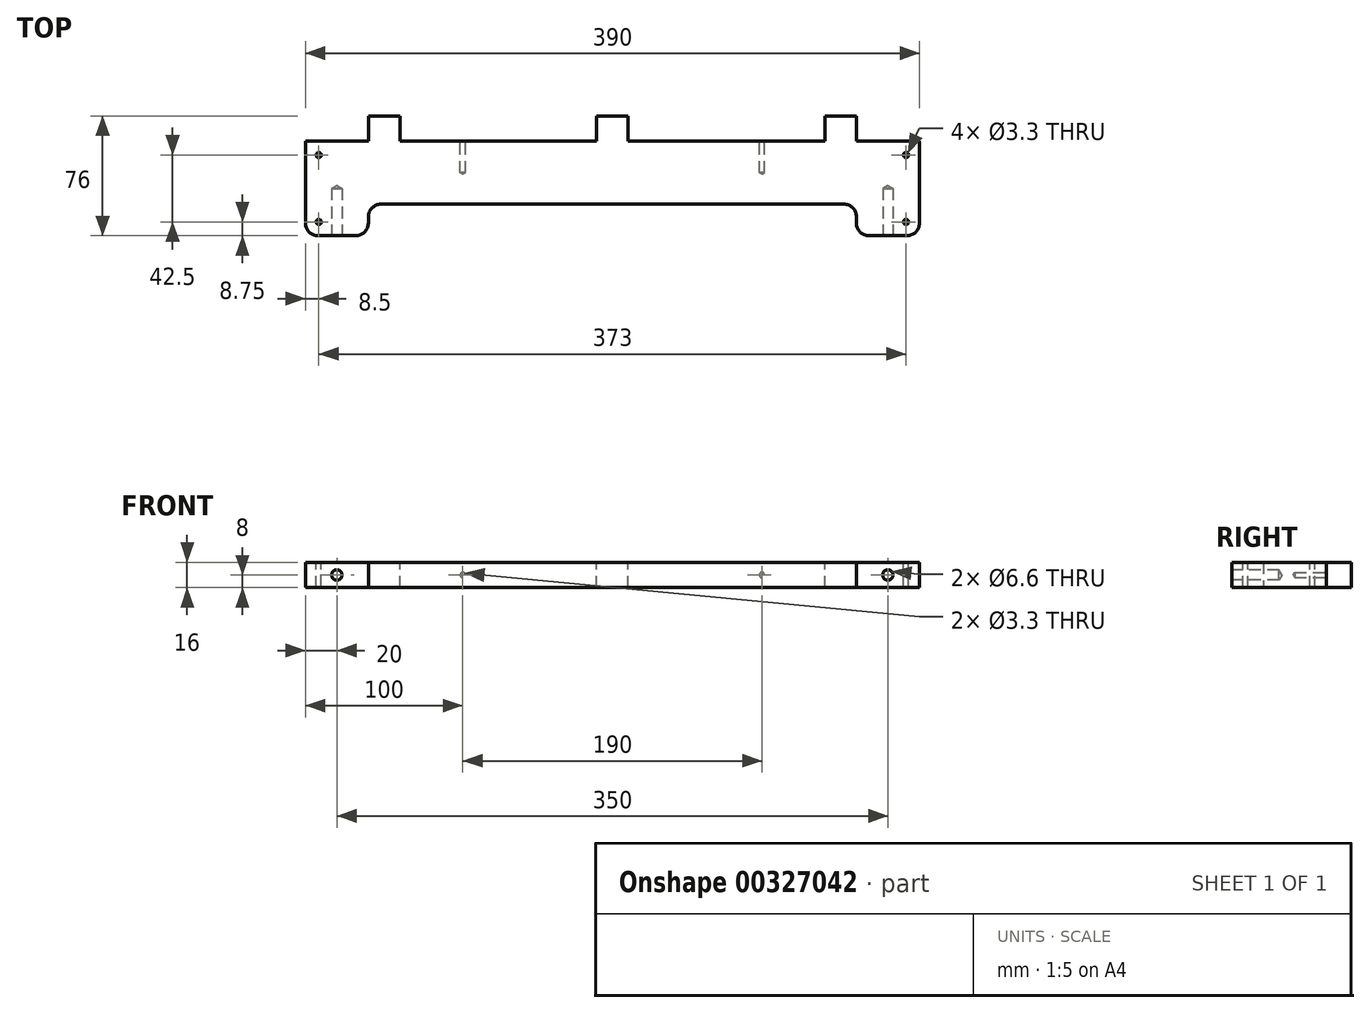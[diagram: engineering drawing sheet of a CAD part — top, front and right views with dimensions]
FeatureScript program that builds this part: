
annotation { "Feature Type Name" : "Feature", "Feature Type Description" : "" }
export const myFeature = defineFeature(function(context is Context, id is Id, definition is map)
    precondition{}
    {
        {
            var Q0;
            Q0=qCreatedBy(makeId("Top.planeOp"),FACE);
            var sketch = newSketch(context, id + "F0", { "sketchPlane" : qUnion([Q0])});
            skLineSegment(sketch, "E0.bottom", {"start": v(195, 20) * mm, "end": v(-195, 20) * mm});
            skLineSegment(sketch, "E0.top", {"start": v(195, -20) * mm, "end": v(-195, -20) * mm});
            skLineSegment(sketch, "E0.left", {"start": v(195, 20) * mm, "end": v(195, -20) * mm});
            skLineSegment(sketch, "E0.right", {"start": v(-195, 20) * mm, "end": v(-195, -20) * mm});
            skPoint(sketch, "E0.middle", {"position": v(0, 0) * mm});
            skLineSegment(sketch, "E1", {"start": v(-195, -20) * mm, "end": v(-195, -40) * mm});
            skLineSegment(sketch, "E2", {"start": v(-195, -40) * mm, "end": v(-155, -40) * mm});
            skLineSegment(sketch, "E3", {"start": v(-155, -40) * mm, "end": v(-155, -20) * mm});
            skLineSegment(sketch, "E4.MirrorCS", {"start": v(195, -40) * mm, "end": v(155, -40) * mm});
            skLineSegment(sketch, "E5.MirrorCS", {"start": v(155, -40) * mm, "end": v(155, -20) * mm});
            skLineSegment(sketch, "E6.MirrorCS", {"start": v(195, -20) * mm, "end": v(195, -40) * mm});
            skSolve(sketch);
        }
        {
            var Q0;
            Q0=makeQuery(id+"F0.imprint","IMPRINT",FACE,{"disambiguationData":[TD([[makeQuery(id+"F0.imprint","IMPRINT",EDGE,{"derivedFrom":sQuery(id+"F0.wireOp",EDGE,"E0.bottom")}),1.0]])]});
            var Q1;
            {var subQ0=sQuery(id+"F0.wireOp",EDGE,"E1");Q1=makeQuery(id+"F0.imprint","IMPRINT",FACE,{"disambiguationData":[TD([[makeQuery(id+"F0.imprint","IMPRINT",EDGE,{"derivedFrom":subQ0}),1.0]])]});}
            var Q2;
            Q2=makeQuery(id+"F0.imprint","IMPRINT",FACE,{"disambiguationData":[TD([[makeQuery(id+"F0.imprint","IMPRINT",EDGE,{"derivedFrom":sQuery(id+"F0.wireOp",EDGE,"E4.MirrorCS")}),-1.0]])]});
            extrude(context, id + "F1", {"entities" : qUnion([Q0, Q1, Q2]), "depth" : 16 * mm});
        }
        {
            var Q0;
            Q0=makeQuery(id+"F1.opExtrude","CAP_FACE",FACE,{"disambiguationData":[OSD([sQuery(id+"F0.wireOp",EDGE,"E0.bottom"),sQuery(id+"F0.wireOp",EDGE,"E0.top"),sQuery(id+"F0.wireOp",EDGE,"E0.left"),sQuery(id+"F0.wireOp",EDGE,"E0.right"),sQuery(id+"F0.wireOp",EDGE,"E1"),sQuery(id+"F0.wireOp",EDGE,"E2"),sQuery(id+"F0.wireOp",EDGE,"E3"),sQuery(id+"F0.wireOp",EDGE,"E4.MirrorCS"),sQuery(id+"F0.wireOp",EDGE,"E5.MirrorCS"),sQuery(id+"F0.wireOp",EDGE,"E6.MirrorCS")])],"isStart":false});
            var sketch = newSketch(context, id + "F2", { "sketchPlane" : qUnion([Q0])});
            skLineSegment(sketch, "E7", {"start": v(-155, 20) * mm, "end": v(-155, 36) * mm});
            skLineSegment(sketch, "E8", {"start": v(-155, 36) * mm, "end": v(-135, 36) * mm});
            skLineSegment(sketch, "E9", {"start": v(-135, 36) * mm, "end": v(-135, 20) * mm});
            skLineSegment(sketch, "E10", {"start": v(-10, 20) * mm, "end": v(-10, 36) * mm});
            skLineSegment(sketch, "E11", {"start": v(-10, 36) * mm, "end": v(10, 36) * mm});
            skLineSegment(sketch, "E12", {"start": v(10, 36) * mm, "end": v(10, 20) * mm});
            skLineSegment(sketch, "E13", {"start": v(0, 36) * mm, "end": v(0, 0) * mm, "construction": true});
            skLineSegment(sketch, "E14.MirrorCS", {"start": v(135, 36) * mm, "end": v(135, 20) * mm});
            skLineSegment(sketch, "E15.MirrorCS", {"start": v(155, 20) * mm, "end": v(155, 36) * mm});
            skLineSegment(sketch, "E16.MirrorCS", {"start": v(155, 36) * mm, "end": v(135, 36) * mm});
            skSolve(sketch);
        }
        {
            var Q0;
            {var subQ0=sQuery(id+"F2.wireOp",EDGE,"E14.MirrorCS");Q0=makeQuery(id+"F2.imprint","IMPRINT",FACE,{"disambiguationData":[TD([[makeQuery(id+"F2.imprint","IMPRINT",EDGE,{"derivedFrom":subQ0}),1.0]])]});}
            var Q1;
            {var subQ0=sQuery(id+"F2.wireOp",EDGE,"E10");Q1=makeQuery(id+"F2.imprint","IMPRINT",FACE,{"disambiguationData":[TD([[makeQuery(id+"F2.imprint","IMPRINT",EDGE,{"derivedFrom":subQ0}),-1.0]])]});}
            var Q2;
            {var subQ0=sQuery(id+"F2.wireOp",EDGE,"E7");Q2=makeQuery(id+"F2.imprint","IMPRINT",FACE,{"disambiguationData":[TD([[makeQuery(id+"F2.imprint","IMPRINT",EDGE,{"derivedFrom":subQ0}),-1.0]])]});}
            var Q3;
            Q3=makeQuery(id+"F1.opExtrude","CAP_FACE",FACE,{"disambiguationData":[OSD([sQuery(id+"F0.wireOp",EDGE,"E0.bottom"),sQuery(id+"F0.wireOp",EDGE,"E0.top"),sQuery(id+"F0.wireOp",EDGE,"E0.left"),sQuery(id+"F0.wireOp",EDGE,"E0.right"),sQuery(id+"F0.wireOp",EDGE,"E1"),sQuery(id+"F0.wireOp",EDGE,"E2"),sQuery(id+"F0.wireOp",EDGE,"E3"),sQuery(id+"F0.wireOp",EDGE,"E4.MirrorCS"),sQuery(id+"F0.wireOp",EDGE,"E5.MirrorCS"),sQuery(id+"F0.wireOp",EDGE,"E6.MirrorCS")])],"isStart":true});
            extrude(context, id + "F3", {"entities" : qUnion([Q0, Q1, Q2]), "operationType" : NewBodyOperationType.ADD, "endBound" : BoundingType.UP_TO_SURFACE, "oppositeDirection" : true, "endBoundEntityFace" : qUnion([Q3]), "depth" : 25 * mm});
        }
        {
            var Q0;
            Q0=makeQuery(id+"F1.opExtrude","SWEPT_FACE",FACE,{"disambiguationData":[OSD([sQuery(id+"F0.wireOp",EDGE,"E2")])]});
            var sketch = newSketch(context, id + "F4", { "sketchPlane" : qUnion([Q0])});
            skLineSegment(sketch, "E17", {"start": v(-155, 0) * mm, "end": v(-195, 16) * mm});
            skLineSegment(sketch, "E18.0.0", {"start": v(155, 0) * mm, "end": v(195, 0) * mm, "construction": true});
            skLineSegment(sketch, "E18.0.1", {"start": v(195, 0) * mm, "end": v(195, 16) * mm, "construction": true});
            skLineSegment(sketch, "E18.0.2", {"start": v(195, 16) * mm, "end": v(155, 16) * mm, "construction": true});
            skLineSegment(sketch, "E18.0.3", {"start": v(155, 16) * mm, "end": v(155, 0) * mm, "construction": true});
            skLineSegment(sketch, "E19", {"start": v(195, 16) * mm, "end": v(155, 0) * mm});
            skPoint(sketch, "E20", {"position": v(175, 8) * mm});
            skPoint(sketch, "E21", {"position": v(-175, 8) * mm});
            skSolve(sketch);
        }
        {
            var Q0;
            Q0=sQuery(id+"F4.wireOp",VERTEX,"E21");
            var Q1;
            Q1=sQuery(id+"F4.wireOp",VERTEX,"E20");
            var Q2;
            Q2=makeQuery(id+"F1.opExtrude","SWEPT_BODY",BODY,{"disambiguationData":[OSD([sQuery(id+"F0.wireOp",EDGE,"E0.bottom"),sQuery(id+"F0.wireOp",EDGE,"E0.top"),sQuery(id+"F0.wireOp",EDGE,"E0.left"),sQuery(id+"F0.wireOp",EDGE,"E0.right"),sQuery(id+"F0.wireOp",EDGE,"E1"),sQuery(id+"F0.wireOp",EDGE,"E2"),sQuery(id+"F0.wireOp",EDGE,"E3"),sQuery(id+"F0.wireOp",EDGE,"E4.MirrorCS"),sQuery(id+"F0.wireOp",EDGE,"E5.MirrorCS"),sQuery(id+"F0.wireOp",EDGE,"E6.MirrorCS")])]});
            hole(context, id + "F5", {"style" : HoleStyle.SIMPLE, "endStyle" : HoleEndStyle.BLIND, "standardTappedOrClearance" : lookupTablePath({ "standard" : "ISO", "fit" : "Normal", "size" : "M6", "type" : "Clearance" }), "standardBlindInLast" : lookupTablePath({ "fit" : "Standard", "standard" : "ISO", "size" : "M6", "type" : "Clearance" }), "holeDiameter" : 6.6 * mm, "holeDepth" : 30 * mm, "tappedDepth" : 12 * mm, "tapClearance" : 3, "locations" : qUnion([Q0, Q1]), "scope" : qUnion([Q2])});
        }
        {
            var Q0;
            Q0=makeQuery(id+"F1.opExtrude","SWEPT_EDGE",EDGE,{"disambiguationData":[OSD([sQuery(id+"F0.wireOp",EDGE,"E2"),sQuery(id+"F0.wireOp",EDGE,"E3")])]});
            var Q1;
            Q1=makeQuery(id+"F1.opExtrude","SWEPT_EDGE",EDGE,{"disambiguationData":[OSD([sQuery(id+"F0.wireOp",EDGE,"E0.top"),sQuery(id+"F0.wireOp",EDGE,"E3")])]});
            var Q2;
            Q2=makeQuery(id+"F1.opExtrude","SWEPT_EDGE",EDGE,{"disambiguationData":[OSD([sQuery(id+"F0.wireOp",EDGE,"E1"),sQuery(id+"F0.wireOp",EDGE,"E2")])]});
            var Q3;
            Q3=makeQuery(id+"F1.opExtrude","SWEPT_EDGE",EDGE,{"disambiguationData":[OSD([sQuery(id+"F0.wireOp",EDGE,"E4.MirrorCS"),sQuery(id+"F0.wireOp",EDGE,"E6.MirrorCS")])]});
            var Q4;
            Q4=makeQuery(id+"F1.opExtrude","SWEPT_EDGE",EDGE,{"disambiguationData":[OSD([sQuery(id+"F0.wireOp",EDGE,"E4.MirrorCS"),sQuery(id+"F0.wireOp",EDGE,"E5.MirrorCS")])]});
            var Q5;
            Q5=makeQuery(id+"F1.opExtrude","SWEPT_EDGE",EDGE,{"disambiguationData":[OSD([sQuery(id+"F0.wireOp",EDGE,"E0.top"),sQuery(id+"F0.wireOp",EDGE,"E5.MirrorCS")])]});
            fillet(context, id + "F6", {"entities" : qUnion([Q0, Q1, Q2, Q3, Q4, Q5]), "radius" : 8 * mm, "tangentPropagation" : true, "allowEdgeOverflow" : false});
        }
        {
            var Q0;
            {var subQ0=sQuery(id+"F2.wireOp",EDGE,"E9");var subQ3=sQuery(id+"F0.wireOp",EDGE,"E0.bottom");Q0=makeQuery(id+"F3.boolean.opBoolean","SPLIT",FACE,{"disambiguationData":[TD([makeQuery(id+"F3.opExtrude","SWEPT_FACE",FACE,{"disambiguationData":[OSD([subQ0])]})])],"derivedFrom":makeQuery(id+"F1.opExtrude","SWEPT_FACE",FACE,{"disambiguationData":[OSD([subQ3])]})});}
            var sketch = newSketch(context, id + "F7", { "sketchPlane" : qUnion([Q0])});
            skLineSegment(sketch, "E22", {"start": v(135, 8) * mm, "end": v(95, 8) * mm});
            skLineSegment(sketch, "E23.0", {"start": v(-135, 0) * mm, "end": v(-135, 16) * mm});
            skLineSegment(sketch, "E24", {"start": v(-135, 8) * mm, "end": v(-95, 8) * mm});
            skSolve(sketch);
        }
        {
            var Q0;
            Q0=sQuery(id+"F7.wireOp",VERTEX,"E22.end");
            var Q1;
            Q1=sQuery(id+"F7.wireOp",VERTEX,"E24.end");
            var Q2;
            Q2=makeQuery(id+"F1.opExtrude","SWEPT_BODY",BODY,{"disambiguationData":[OSD([sQuery(id+"F0.wireOp",EDGE,"E0.bottom"),sQuery(id+"F0.wireOp",EDGE,"E0.top"),sQuery(id+"F0.wireOp",EDGE,"E0.left"),sQuery(id+"F0.wireOp",EDGE,"E0.right"),sQuery(id+"F0.wireOp",EDGE,"E1"),sQuery(id+"F0.wireOp",EDGE,"E2"),sQuery(id+"F0.wireOp",EDGE,"E3"),sQuery(id+"F0.wireOp",EDGE,"E4.MirrorCS"),sQuery(id+"F0.wireOp",EDGE,"E5.MirrorCS"),sQuery(id+"F0.wireOp",EDGE,"E6.MirrorCS")])]});
            hole(context, id + "F8", {"style" : HoleStyle.SIMPLE, "endStyle" : HoleEndStyle.BLIND, "standardTappedOrClearance" : lookupTablePath({ "standard" : "ISO", "fit" : "Normal", "size" : "M3", "type" : "Clearance" }), "standardBlindInLast" : lookupTablePath({ "fit" : "Standard", "standard" : "ISO", "size" : "M3", "type" : "Clearance" }), "holeDiameter" : 3.3 * mm, "holeDepth" : 20 * mm, "tappedDepth" : 12 * mm, "tapClearance" : 3, "locations" : qUnion([Q0, Q1]), "scope" : qUnion([Q2])});
        }
        {
            var Q0;
            {var subQ0=sQuery(id+"F0.wireOp",EDGE,"E0.bottom");Q0=makeQuery(id+"F3.boolean.opBoolean","MERGE",FACE,{"derivedFrom":[makeQuery(id+"F1.opExtrude","CAP_FACE",FACE,{"disambiguationData":[OSD([subQ0,sQuery(id+"F0.wireOp",EDGE,"E0.top"),sQuery(id+"F0.wireOp",EDGE,"E0.left"),sQuery(id+"F0.wireOp",EDGE,"E0.right"),sQuery(id+"F0.wireOp",EDGE,"E1"),sQuery(id+"F0.wireOp",EDGE,"E2"),sQuery(id+"F0.wireOp",EDGE,"E3"),sQuery(id+"F0.wireOp",EDGE,"E4.MirrorCS"),sQuery(id+"F0.wireOp",EDGE,"E5.MirrorCS"),sQuery(id+"F0.wireOp",EDGE,"E6.MirrorCS")])],"isStart":false}),makeQuery(id+"F3.opExtrude","CAP_FACE",FACE,{"disambiguationData":[OSD([subQ0,sQuery(id+"F2.wireOp",EDGE,"E7"),sQuery(id+"F2.wireOp",EDGE,"E8"),sQuery(id+"F2.wireOp",EDGE,"E9")])],"isStart":true}),makeQuery(id+"F3.opExtrude","CAP_FACE",FACE,{"disambiguationData":[OSD([subQ0,sQuery(id+"F2.wireOp",EDGE,"E10"),sQuery(id+"F2.wireOp",EDGE,"E11"),sQuery(id+"F2.wireOp",EDGE,"E12")])],"isStart":true}),makeQuery(id+"F3.opExtrude","CAP_FACE",FACE,{"disambiguationData":[OSD([subQ0,sQuery(id+"F2.wireOp",EDGE,"E14.MirrorCS"),sQuery(id+"F2.wireOp",EDGE,"E15.MirrorCS"),sQuery(id+"F2.wireOp",EDGE,"E16.MirrorCS")])],"isStart":true})]});}
            var sketch = newSketch(context, id + "F9", { "sketchPlane" : qUnion([Q0])});
            skLineSegment(sketch, "E25", {"start": v(-186.5, -40) * mm, "end": v(-186.5, -31.25) * mm});
            skLineSegment(sketch, "E26", {"start": v(-186.5, -31.25) * mm, "end": v(-186.5, 11.25) * mm});
            skLineSegment(sketch, "E27", {"start": v(0, -20) * mm, "end": v(0, 36) * mm, "construction": true});
            skLineSegment(sketch, "E28.MirrorCS", {"start": v(186.5, -40) * mm, "end": v(186.5, -31.25) * mm});
            skLineSegment(sketch, "E29.MirrorCS", {"start": v(186.5, -31.25) * mm, "end": v(186.5, 11.25) * mm});
            skSolve(sketch);
        }
        {
            var Q0;
            Q0=sQuery(id+"F9.wireOp",VERTEX,"E26.end");
            var Q1;
            Q1=sQuery(id+"F9.wireOp",VERTEX,"E26.start");
            var Q2;
            Q2=sQuery(id+"F9.wireOp",VERTEX,"E29.MirrorCS.end");
            var Q3;
            Q3=sQuery(id+"F9.wireOp",VERTEX,"E29.MirrorCS.start");
            var Q4;
            Q4=makeQuery(id+"F1.opExtrude","SWEPT_BODY",BODY,{"disambiguationData":[OSD([sQuery(id+"F0.wireOp",EDGE,"E0.bottom"),sQuery(id+"F0.wireOp",EDGE,"E0.top"),sQuery(id+"F0.wireOp",EDGE,"E0.left"),sQuery(id+"F0.wireOp",EDGE,"E0.right"),sQuery(id+"F0.wireOp",EDGE,"E1"),sQuery(id+"F0.wireOp",EDGE,"E2"),sQuery(id+"F0.wireOp",EDGE,"E3"),sQuery(id+"F0.wireOp",EDGE,"E4.MirrorCS"),sQuery(id+"F0.wireOp",EDGE,"E5.MirrorCS"),sQuery(id+"F0.wireOp",EDGE,"E6.MirrorCS")])]});
            hole(context, id + "F10", {"style" : HoleStyle.SIMPLE, "endStyle" : HoleEndStyle.THROUGH, "standardTappedOrClearance" : lookupTablePath({ "standard" : "ISO", "fit" : "Normal", "size" : "M3", "type" : "Clearance" }), "standardBlindInLast" : lookupTablePath({ "fit" : "Standard", "standard" : "ISO", "size" : "M3", "type" : "Clearance" }), "holeDiameter" : 3.3 * mm, "tappedDepth" : 12 * mm, "tapClearance" : 3, "locations" : qUnion([Q0, Q1, Q2, Q3]), "scope" : qUnion([Q4])});
        }
    });
